# Revit family: 3456A_NX_Smart_Port
name_source: partatom
category: Communication Devices
revit_build: Autodesk Revit 2014 (Build: 20130308_1515(x64)
units: mm (PartAtom-declared; Revit-internal decimal feet)

## types (1)
- 3456A_NX_Smart_Port
    Apparent Load = 0 VA
    Assembly Code = D5090
    Black Material = Paint - Hubbell - Black Matte Textured
    Default Elevation = 48 "
    Description = The NX SmartPORT Module provides easy access to connect smart switch stations, motion detectors, and daylight sensors into a NX network system
    Featrues = Connects to the HubbNET™ network through the NXHDI
Device Network Interface Module
• Four independent SmartPORT connectors, each with two
RJ45 connectors
• Compatible with all NX Smart Switch Stations, NX Occupancy
Sensors and NX Daylight Sensor
• Mounts to standard DIN rail
    Green Element = Plastic - Hubbell - Green
    Manufacturer = Hubbell Control Solutions
    Model = NX SmartPORT Module
    Product Page URL = https://www.hubbell.com
    Product Specification = https://hubbellcdn.com
    Steel = Metal-Hubbell-Galvanized_Steel
    Type Comments = NX SmartPORT Module
    URL = https://www.hubbell.com
    Voltage = 24 V
    Warranty = 5-Years Warranty
    White Element = Glass, White, High Luminance

## geometry (parser evidence)
native form markers: Sweep x1
no freeform markers — native parametric forms only
